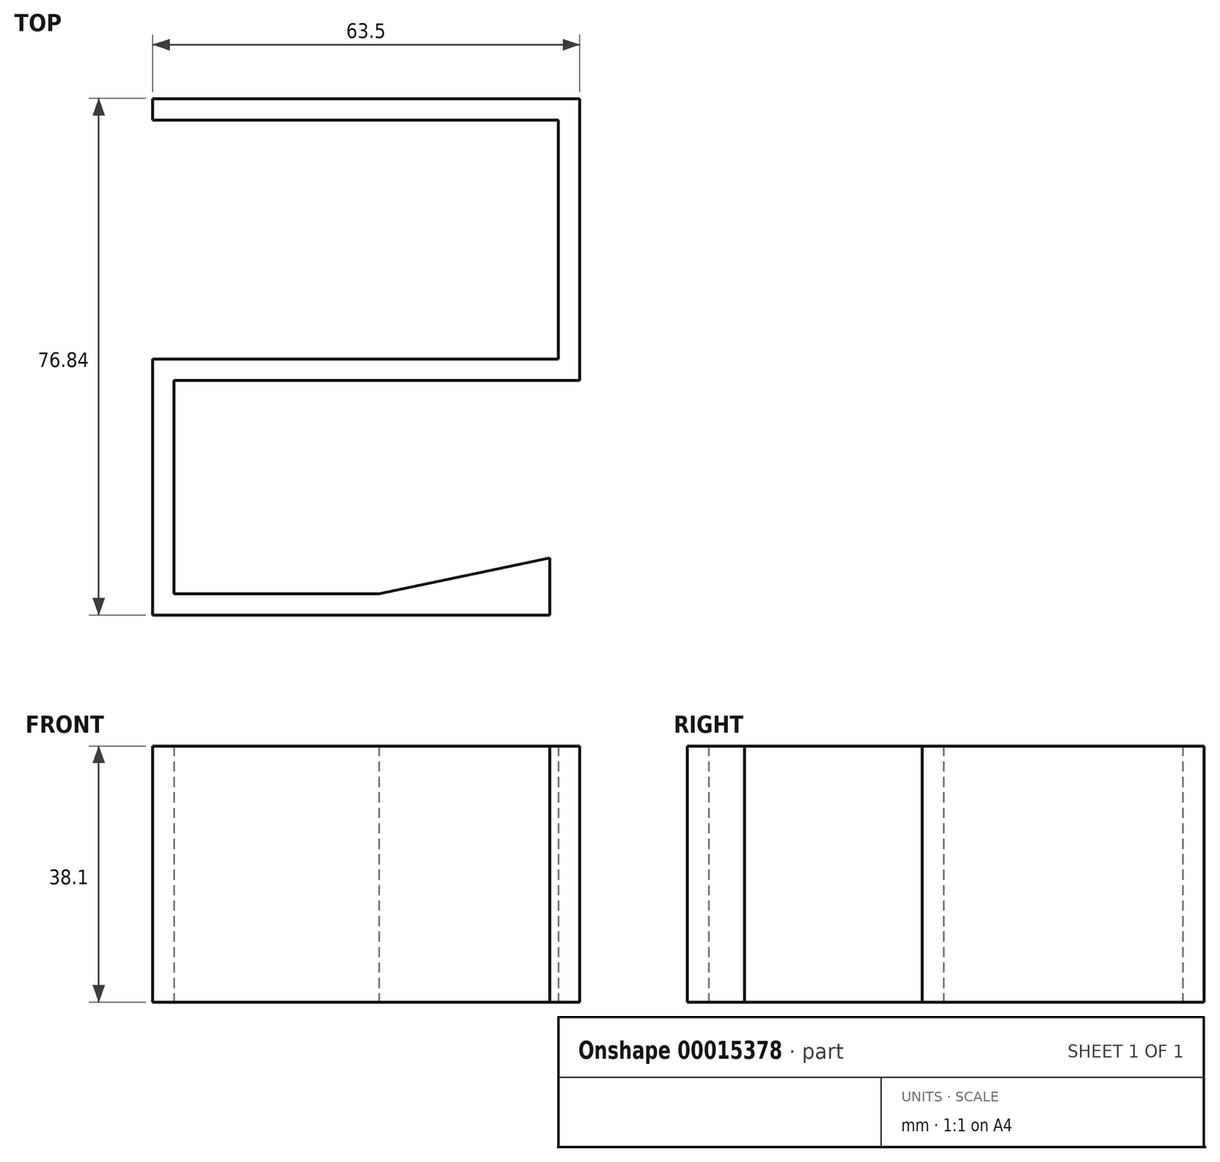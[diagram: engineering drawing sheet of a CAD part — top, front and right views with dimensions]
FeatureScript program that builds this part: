
annotation { "Feature Type Name" : "Feature", "Feature Type Description" : "" }
export const myFeature = defineFeature(function(context is Context, id is Id, definition is map)
    precondition{}
    {
        {
            var Q0;
            Q0=qCreatedBy(makeId("Top.planeOp"),FACE);
            var sketch = newSketch(context, id + "F0", { "sketchPlane" : qUnion([Q0])});
            skLineSegment(sketch, "E0", {"start": v(0, 0) * mm, "end": v(60.33, 0) * mm});
            skLineSegment(sketch, "E1", {"start": v(60.33, 0) * mm, "end": v(60.33, -35.56) * mm});
            skLineSegment(sketch, "E2", {"start": v(60.33, -35.56) * mm, "end": v(0, -35.56) * mm});
            skLineSegment(sketch, "E3", {"start": v(0, -35.56) * mm, "end": v(0, -73.66) * mm});
            skLineSegment(sketch, "E4", {"start": v(0, -73.66) * mm, "end": v(59.06, -73.66) * mm});
            skLineSegment(sketch, "E5", {"start": v(59.06, -73.66) * mm, "end": v(59.06, -65.2) * mm});
            skLineSegment(sketch, "E6", {"start": v(59.06, -65.2) * mm, "end": v(33.66, -70.49) * mm});
            skLineSegment(sketch, "E7", {"start": v(33.66, -70.49) * mm, "end": v(3.18, -70.49) * mm});
            skLineSegment(sketch, "E8", {"start": v(3.17, -70.49) * mm, "end": v(3.17, -38.74) * mm});
            skLineSegment(sketch, "E9", {"start": v(3.17, -38.74) * mm, "end": v(63.5, -38.74) * mm});
            skLineSegment(sketch, "E10", {"start": v(63.5, -38.74) * mm, "end": v(63.5, 3.18) * mm});
            skLineSegment(sketch, "E11", {"start": v(63.5, 3.18) * mm, "end": v(0, 3.18) * mm});
            skLineSegment(sketch, "E12", {"start": v(0, 3.18) * mm, "end": v(0, 0) * mm});
            skSolve(sketch);
        }
        {
            var Q0;
            Q0=qSketchRegion(id+"F0",true);
            extrude(context, id + "F1", {"entities" : qUnion([Q0]), "depth" : 38.1 * mm});
        }
    });
